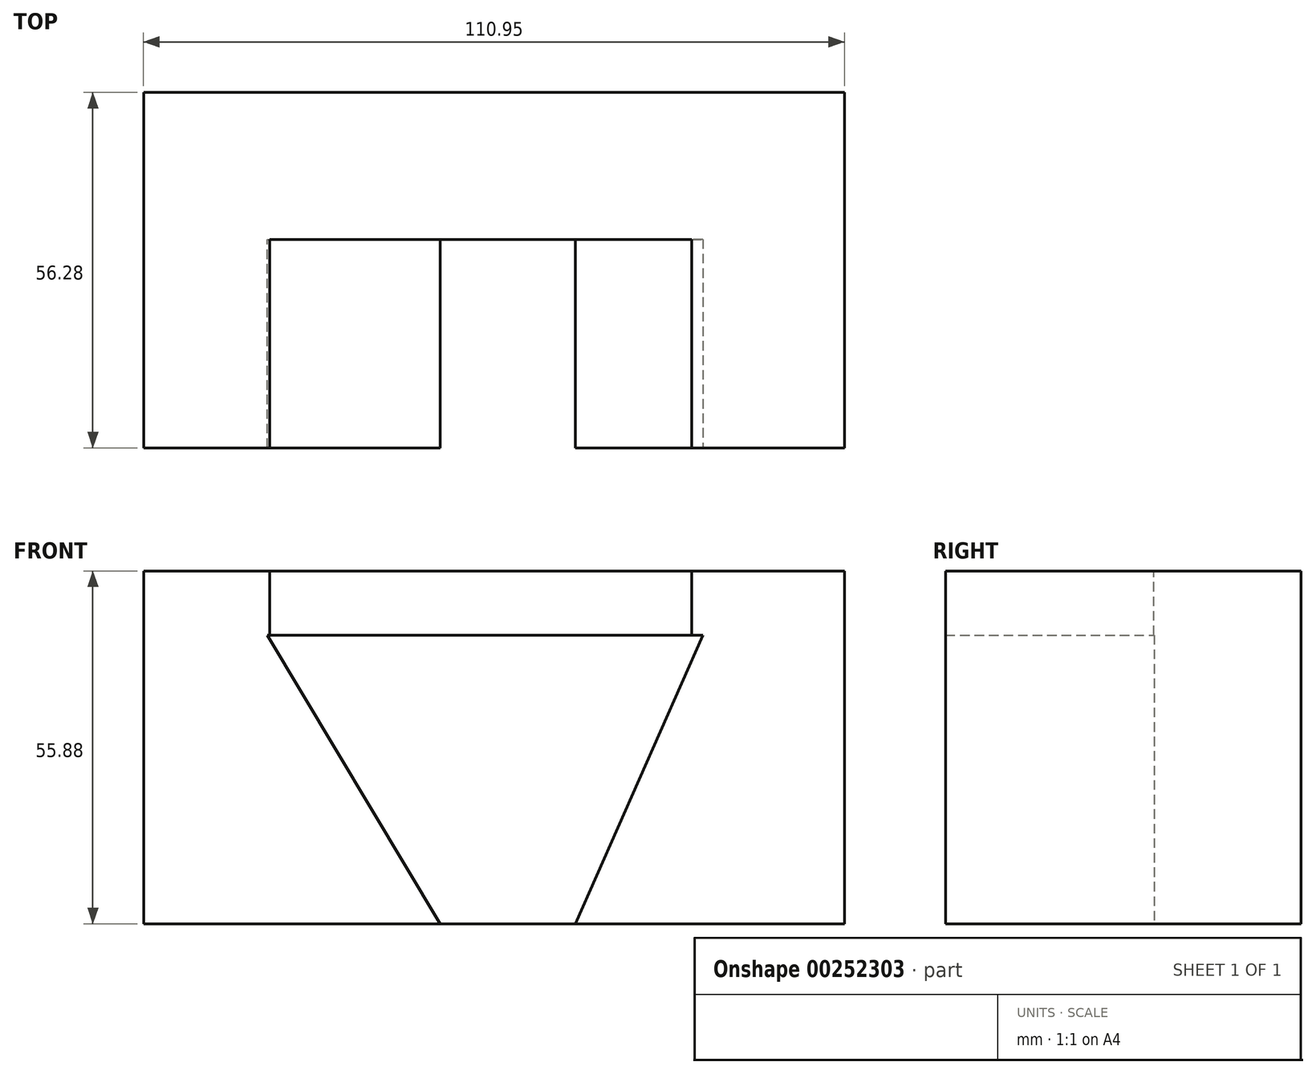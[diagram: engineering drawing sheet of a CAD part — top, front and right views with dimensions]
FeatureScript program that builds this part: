
annotation { "Feature Type Name" : "Feature", "Feature Type Description" : "" }
export const myFeature = defineFeature(function(context is Context, id is Id, definition is map)
    precondition{}
    {
        {
            var Q0;
            Q0=qCreatedBy(makeId("Top.planeOp"),FACE);
            var sketch = newSketch(context, id + "F0", { "sketchPlane" : qUnion([Q0])});
            skLineSegment(sketch, "E0.bottom", {"start": v(-52.22, 23.72) * mm, "end": v(58.73, 23.72) * mm});
            skLineSegment(sketch, "E0.top", {"start": v(-52.22, -32.56) * mm, "end": v(58.73, -32.56) * mm});
            skLineSegment(sketch, "E0.left", {"start": v(-52.22, 23.72) * mm, "end": v(-52.22, -32.56) * mm});
            skLineSegment(sketch, "E0.right", {"start": v(58.73, 23.72) * mm, "end": v(58.73, -32.56) * mm});
            skSolve(sketch);
        }
        {
            var Q0;
            Q0=makeQuery(id+"F0.imprint","IMPRINT",FACE,{"disambiguationData":[TD([[makeQuery(id+"F0.imprint","IMPRINT",EDGE,{"derivedFrom":sQuery(id+"F0.wireOp",EDGE,"E0.bottom")}),-1.0]])]});
            extrude(context, id + "F1", {"entities" : qUnion([Q0]), "depth" : 55.88 * mm});
        }
        {
            var Q0;
            Q0=makeQuery(id+"F1.opExtrude","SWEPT_FACE",FACE,{"disambiguationData":[OSD([sQuery(id+"F0.wireOp",EDGE,"E0.top")])]});
            var sketch = newSketch(context, id + "F2", { "sketchPlane" : qUnion([Q0])});
            skLineSegment(sketch, "E1", {"start": v(-33.38, 46.98) * mm, "end": v(-5.23, 0) * mm});
            skLineSegment(sketch, "E2", {"start": v(16.16, 0) * mm, "end": v(36.87, 46.98) * mm});
            skLineSegment(sketch, "E3", {"start": v(36.87, 46.98) * mm, "end": v(-33.38, 46.98) * mm});
            skSolve(sketch);
        }
        {
            var Q0;
            {var subQ0=sQuery(id+"F2.wireOp",EDGE,"E1");Q0=makeQuery(id+"F2.imprint","IMPRINT",FACE,{"disambiguationData":[TD([[makeQuery(id+"F2.imprint","IMPRINT",EDGE,{"derivedFrom":subQ0}),1.0]])]});}
            extrude(context, id + "F3", {"entities" : qUnion([Q0]), "operationType" : NewBodyOperationType.REMOVE, "oppositeDirection" : true, "depth" : 33.02 * mm});
        }
        {
            var Q0;
            Q0=makeQuery(id+"F1.opExtrude","CAP_FACE",FACE,{"disambiguationData":[OSD([sQuery(id+"F0.wireOp",EDGE,"E0.bottom"),sQuery(id+"F0.wireOp",EDGE,"E0.top"),sQuery(id+"F0.wireOp",EDGE,"E0.left"),sQuery(id+"F0.wireOp",EDGE,"E0.right")])],"isStart":false});
            var sketch = newSketch(context, id + "F4", { "sketchPlane" : qUnion([Q0])});
            skLineSegment(sketch, "E4.bottom", {"start": v(-34.77, -32.56) * mm, "end": v(37.1, -32.56) * mm});
            skLineSegment(sketch, "E4.top", {"start": v(-34.77, 10.56) * mm, "end": v(37.1, 10.56) * mm});
            skLineSegment(sketch, "E4.left", {"start": v(-34.77, -32.56) * mm, "end": v(-34.77, 10.56) * mm});
            skLineSegment(sketch, "E4.right", {"start": v(37.1, -32.56) * mm, "end": v(37.1, 10.56) * mm});
            skSolve(sketch);
        }
        {
            var Q0;
            Q0=makeQuery(id+"F4.imprint","IMPRINT",FACE,{"disambiguationData":[TD([[makeQuery(id+"F4.imprint","IMPRINT",EDGE,{"derivedFrom":sQuery(id+"F4.wireOp",EDGE,"E4.bottom")}),1.0]])]});
            extrude(context, id + "F5", {"entities" : qUnion([Q0]), "operationType" : NewBodyOperationType.REMOVE, "oppositeDirection" : true, "depth" : 10.16 * mm});
        }
        {
            var Q0;
            Q0=makeQuery(id+"F5.boolean.opBoolean","COPY",FACE,{"derivedFrom":makeQuery(id+"F5.opExtrude","SWEPT_FACE",FACE,{"disambiguationData":[OSD([sQuery(id+"F4.wireOp",EDGE,"E4.left")])]})});
            extrude(context, id + "F6", {"entities" : qUnion([Q0]), "operationType" : NewBodyOperationType.ADD, "depth" : 2.54 * mm});
        }
        {
            var Q0;
            Q0=makeQuery(id+"F5.boolean.opBoolean","COPY",FACE,{"derivedFrom":makeQuery(id+"F5.opExtrude","SWEPT_FACE",FACE,{"disambiguationData":[OSD([sQuery(id+"F4.wireOp",EDGE,"E4.top")])]})});
            extrude(context, id + "F7", {"entities" : qUnion([Q0]), "operationType" : NewBodyOperationType.ADD, "depth" : 10.16 * mm});
        }
        {
            var Q0;
            Q0=makeQuery(id+"F5.boolean.opBoolean","COPY",FACE,{"derivedFrom":makeQuery(id+"F5.opExtrude","SWEPT_FACE",FACE,{"disambiguationData":[OSD([sQuery(id+"F4.wireOp",EDGE,"E4.right")])]})});
            extrude(context, id + "F8", {"entities" : qUnion([Q0]), "operationType" : NewBodyOperationType.ADD, "depth" : 2.54 * mm});
        }
    });
